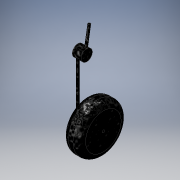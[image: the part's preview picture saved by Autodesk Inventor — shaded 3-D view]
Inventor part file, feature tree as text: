
AUTODESK INVENTOR PART (.ipt)
format: ipt  version: 2018 (Build 220112000, 112)  size: 177,152 bytes
history: native  units: in
note: dims shown in document units (in); Inventor stores cm internally (conversion verified against a paired STEP export)
features: sketch x5, plane x3, extrude x2, sweep x2, fillet x1
ambient origin geometry x8: Origin, YZ Plane, XZ Plane, XY Plane, X Axis, Y Axis, Z Axis, Center Point
bodies: Solid1 (feature_tree), Solid2 (feature_tree)
feature tree (13):
  sketch  "3D Sketch1"
  plane  "Work Plane1"
  extrude  "Extrusion1"  Depth=3.5827in
  plane  "Work Plane2"
  sketch  "Sketch2"  dims[d2=0.4528in d3=0.7047in]
  plane  "Work Plane3"
  sweep  "Sweep1"
  sweep  "Sweep2"
  extrude  "Extrusion2"  TaperAngle=0.0deg  [1 undecoded]
  fillet  "Fillet1"  [1 undecoded]
  sketch  "Sketch1"  dims[d0=1.5866in d1=3.5827in]
  sketch  "Sketch3"  dims[d4=0.5512in d5=0.0in d6=0.1575in]
  sketch  "Sketch4"  dims[d7=0.1575in d8=0.0in d9=0.0in d10=0.0in d11=0.0in d12=3.0in d13=1.063in d14=0.0in d15=0.3937in]
note: 2 required parameter values undecoded (feature->parameter linkage not recoverable at this tier; creation-order binding heuristic only, values carry confidence <= 0.55)
